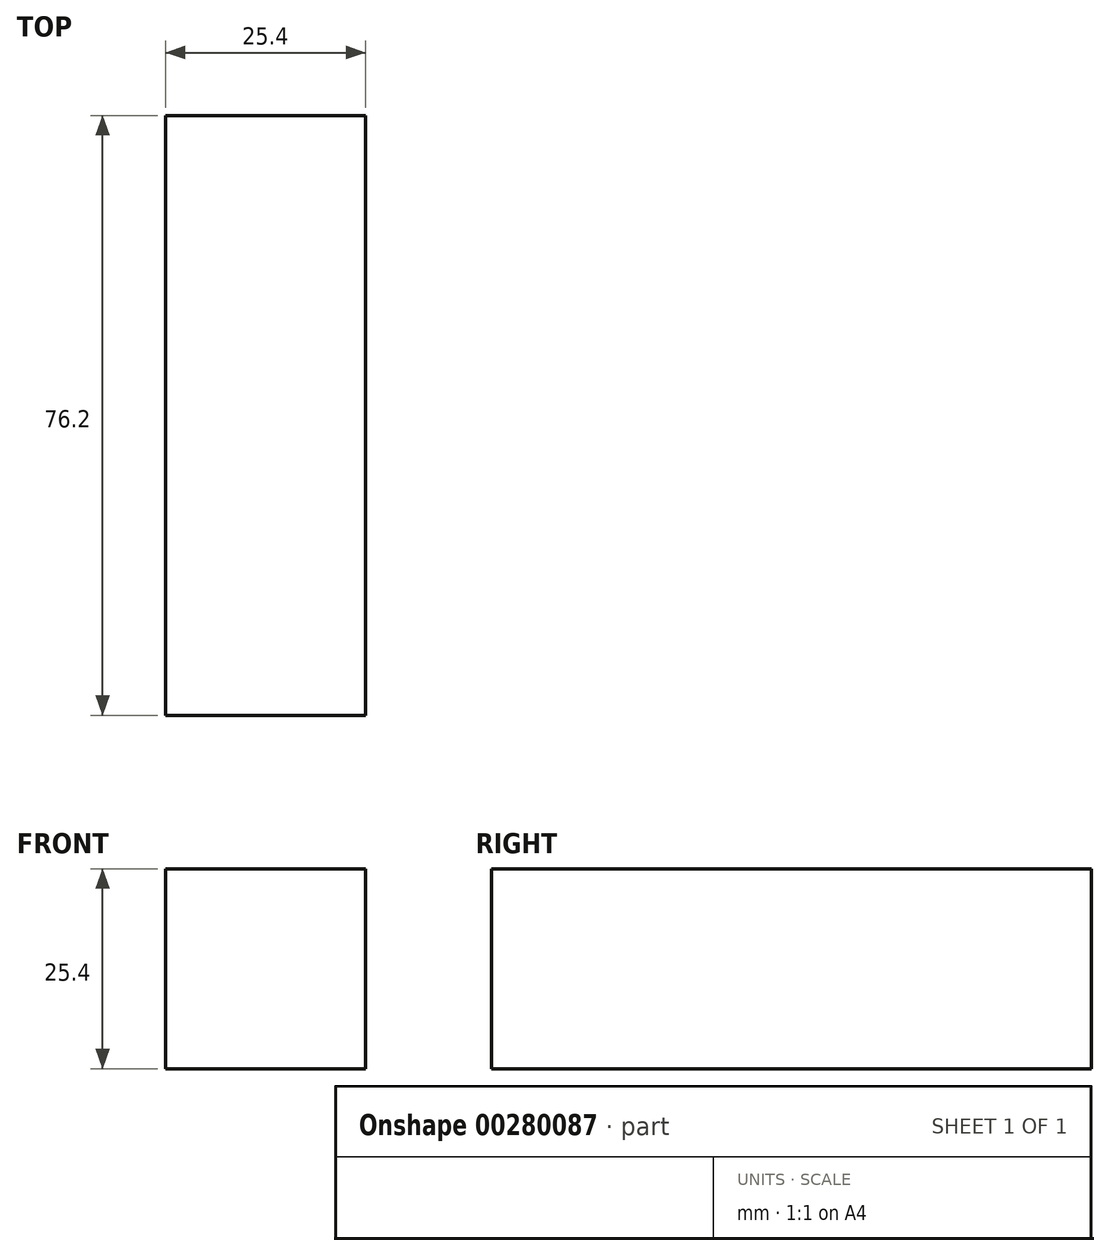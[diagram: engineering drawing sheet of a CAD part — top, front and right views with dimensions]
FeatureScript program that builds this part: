
annotation { "Feature Type Name" : "Feature", "Feature Type Description" : "" }
export const myFeature = defineFeature(function(context is Context, id is Id, definition is map)
    precondition{}
    {
        {
            var Q0;
            Q0=qCreatedBy(makeId("Front.planeOp"),FACE);
            var sketch = newSketch(context, id + "F0", { "sketchPlane" : qUnion([Q0])});
            skLineSegment(sketch, "E0.bottom", {"start": v(-25.4, 25.4) * mm, "end": v(0, 25.4) * mm});
            skLineSegment(sketch, "E0.top", {"start": v(-25.4, 0) * mm, "end": v(0, 0) * mm});
            skLineSegment(sketch, "E0.left", {"start": v(-25.4, 25.4) * mm, "end": v(-25.4, 0) * mm});
            skLineSegment(sketch, "E0.right", {"start": v(0, 25.4) * mm, "end": v(0, 0) * mm});
            skSolve(sketch);
        }
        {
            var Q0;
            Q0 = qSketchRegion(id + "F0", true);
            extrude(context, id + "F1", {"entities" : qUnion([Q0]), "depth" : 76.2 * mm});
        }
    });
